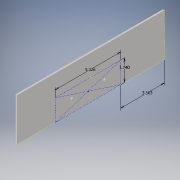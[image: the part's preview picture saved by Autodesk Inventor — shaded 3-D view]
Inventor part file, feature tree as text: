
AUTODESK INVENTOR PART (.ipt)
format: ipt  version: 2017 (Build 210142000, 142)  size: 110,592 bytes
history: native  units: in
note: dims shown in document units (in); Inventor stores cm internally (conversion verified against a paired STEP export)
features: sketch x3, extrude x1, hole x1
ambient origin geometry x8: Origin, YZ Plane, XZ Plane, XY Plane, X Axis, Y Axis, Z Axis, Center Point
bodies: Solid1 (feature_tree)
feature tree (5):
  extrude  "Extrusion1"  Depth=3.47in
  sketch  "Sketch2"  dims[d2=0.125in d3=0.0in d4=5.326in]
  hole  "Hole1"  [1 undecoded]
  sketch  "Sketch1"  dims[d0=12.0in d1=3.47in]
  sketch  "Sketch3"  dims[d5=1.74in d6=3.5625in d7=1.035in d8=1.332in d9=1.332in d10=0.177in d11=0.75in d12=0.409in d13=0.25in d14=90.0deg d15=1.0in d16=0.8108in]
note: 1 required parameter value undecoded (feature->parameter linkage not recoverable at this tier; creation-order binding heuristic only, values carry confidence <= 0.55)
